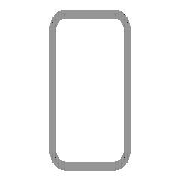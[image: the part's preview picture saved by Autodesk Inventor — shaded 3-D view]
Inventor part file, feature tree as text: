
AUTODESK INVENTOR PART (.ipt)
format: ipt  version: 2025 (Build 290162010, 162A)  size: 131,072 bytes
history: native  units: mm (DEFAULTED — no unit token found)
features: other x3, sketch x1, plane x1
ambient origin geometry x8: Origin, YZ Plane, XZ Plane, XY Plane, X Axis, Y Axis, Z Axis, Center Point
bodies: Solid1 (feature_tree), Body (feature_tree)
feature tree (5):
  other  "Driven Length"
  other  "Start plane"
  other  "End plane"
  sketch  "Sketch3"  dims[d3=1270.0mm d4=0.0mm d7=6.0mm d9=40.0mm d11=60.0mm d12=3.0mm d13=-0.0mm d14=1270.0mm d15=20.0mm d16=30.0mm d17=90.0deg d18=1270.0mm]
  plane  "Work Plane3"
